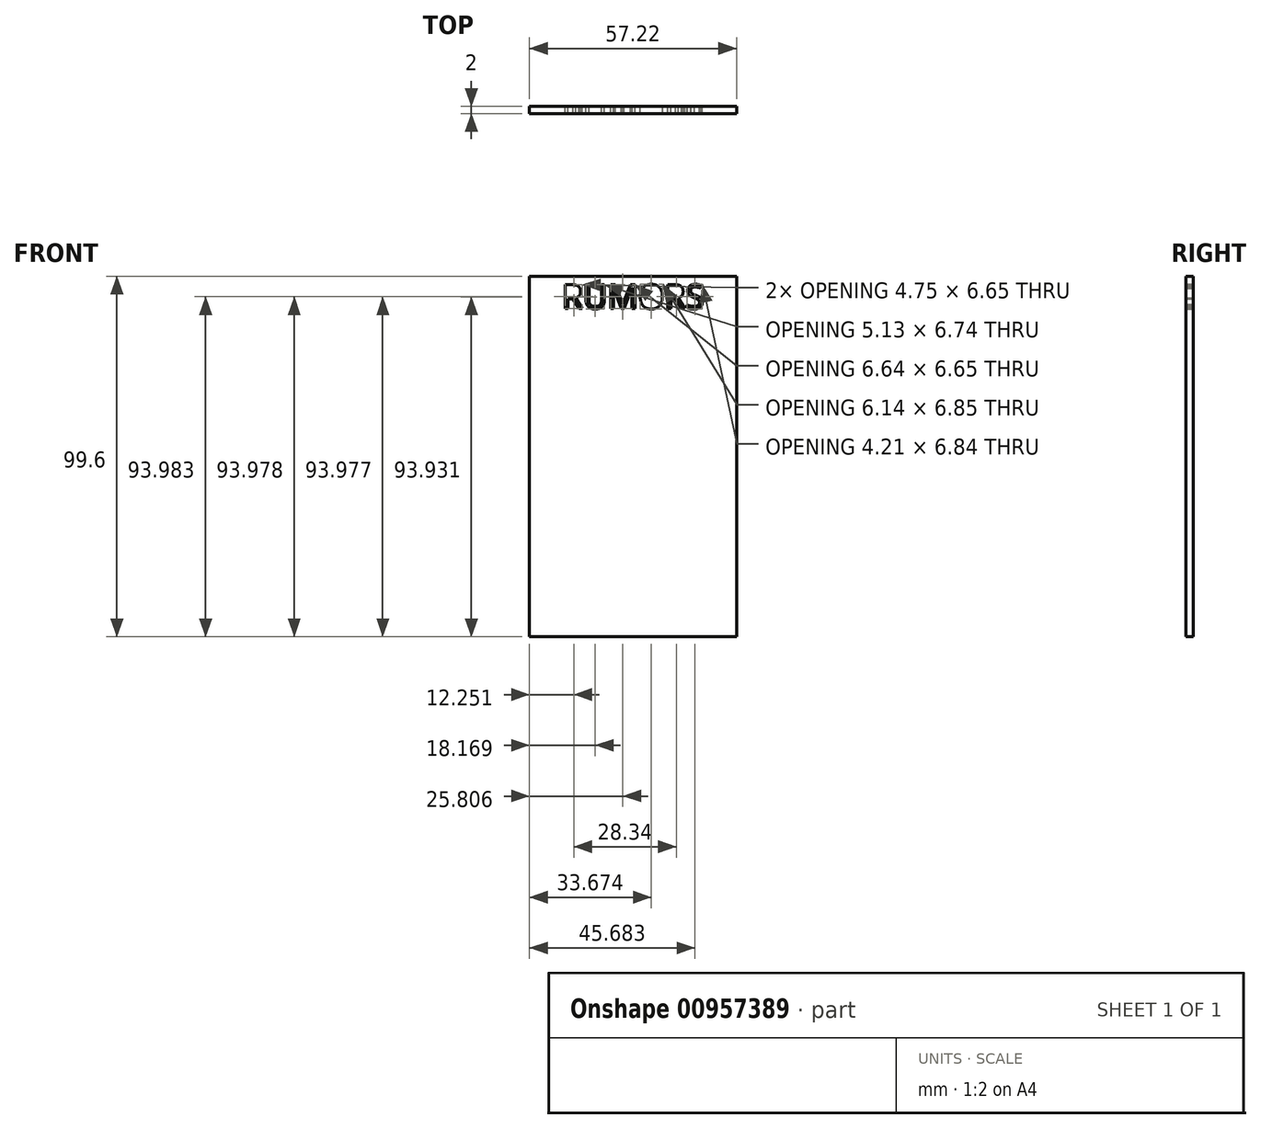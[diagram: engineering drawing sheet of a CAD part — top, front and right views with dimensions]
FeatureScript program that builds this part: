
annotation { "Feature Type Name" : "Feature", "Feature Type Description" : "" }
export const myFeature = defineFeature(function(context is Context, id is Id, definition is map)
    precondition{}
    {
        {
            var Q0;
            Q0=qCreatedBy(makeId("Front.planeOp"),FACE);
            var sketch = newSketch(context, id + "F0", { "sketchPlane" : qUnion([Q0])});
            skLineSegment(sketch, "E0.bottom", {"start": v(-57.22, 26.21) * mm, "end": v(0, 26.21) * mm});
            skLineSegment(sketch, "E0.top", {"start": v(-57.22, -73.4) * mm, "end": v(0, -73.4) * mm});
            skLineSegment(sketch, "E0.left", {"start": v(-57.22, 26.21) * mm, "end": v(-57.22, -73.4) * mm});
            skLineSegment(sketch, "E0.right", {"start": v(0, 26.21) * mm, "end": v(0, -73.4) * mm});
            skText(sketch, "E1", { "text": "RUMORS", "fontName": "NotoSans-Regular.ttf"});
            const initialGuessF0  = {"E1": [-0.04825, 0.01726, 1, 0, 0.00671]};
            skSetInitialGuess(sketch, initialGuessF0);
            skSolve(sketch);
        }
        {
            var Q0;
            Q0=makeQuery(id+"F0.imprint","IMPRINT",FACE,{"disambiguationData":[TD([[makeQuery(id+"F0.imprint","IMPRINT",EDGE,{"derivedFrom":sQuery(id+"F0.wireOp",EDGE,"E0.bottom")}),-1.0]])]});
            extrude(context, id + "F1", {"entities" : qUnion([Q0]), "depth" : 2 * mm, "offsetDistance" : 25.4 * mm});
        }
    });
